# Revit family: xJWELED 40M Exit Lighting Non-Hosted_R16
name_source: partatom
category: Lighting Fixtures
revit_build: Autodesk Revit 2016 (Build: 20151007_0715(x64)
units: mm (PartAtom-declared; Revit-internal decimal feet)

## family parameters
Always vertical = Yes
Cut with Voids When Loaded = No
Light Source = Yes
OmniClass Number = 23.80.70.00
OmniClass Title = Lighting
Part Type = Normal
Room Calculation Point = No
Round Connector Dimension = Use Diameter
Shared = No
Work Plane-Based = No

## types (14) — shared parameters
AS2293 Classification = C0=E1.6 C90=E1.25
Base Material Construction = Polycarbonate
Color Filter = 16777215
Cover Material Construction = Clear Polycarbonate
Diffuser = Opal panel
Dimensions (L x W x H) = 560mm x 130mm x 280mm
Dimming Lamp Color Temperature Shift = <None>
Emit Shape Visible in Rendering = No
IK Rating = IK08 (side surface) IK09 (front surface)
IP Rating = IP66/67
Lamp = 4 x 5 high intensity, low energy LED, surface mounted onto a replaceable lamp bar - 100,000hr
Manufacturer = Clevertronics
Mounting = Wall mount
Operating Temperature = 0°C to 40°C
Operating Voltage = 240V AC; 50Hz
Photometric Web File = ll18428a - LJWELED-40-WM-RR.IES
Replacement Emergency Lamp = 8002122 PCA:Duris E5 LED Strip 5LED ,CT10152-D4
Tilt Angle = 0.00°
Total Lumen Output = 74.1
Viewing Distance = 40m
Weight = 5.5Kg

## per-type parameters (varying)
| type | Battery | Battery Type | Charging Method | Description | MIC Number | Operating Mode | Pictogram | Power Consumption | Power Consumption (Standby) | Product Description | Replacement Battery | Replacement Emergency Driver | Testing Node | Testing System |
| LJWELED-40-DALI-WM-E | Lithium Nanophosphate | 3.3V 2500mAh | Intelligent current limited constant voltage | WP LED Exit, WM, MNT,Exit,Dali Reg,L10,40mtr | AUA01220030102 | Maintained | EXIT wording (must specify user combination) | 5.3W | 2.8W | L10 Lithium Nanophosphate wall mount IP66/67 Jumbo weatherproof Exit | 1530010  BATTERY:L10 3.3V 2.5AH 200mm lead, Brkt | LJWELED-40-CKIT  WP LED Exit, Control Kit, L10, OWC | 8003060  PCA: New DALI #CT10629-Ax | DALI registered |
| LJWELED-40-DALI-WM-R | Lithium Nanophosphate | 3.3V 2500mAh | Intelligent current limited constant voltage | WP LED Exit, WM, MNT,RM, Dali Reg,L10, 40mtr | AUA01220040102 | Maintained | Running man (must specify user combination) | 5.3W | 2.8W | L10 Lithium Nanophosphate wall mount IP66/67 Jumbo weatherproof Exit | 1530010  BATTERY:L10 3.3V 2.5AH 200mm lead, Brkt | LJWELED-40-CKIT  WP LED Exit, Control Kit, L10, OWC | 8003060  PCA: New DALI #CT10629-Ax | DALI registered |
| LJWELED-40-DALI-WM-RR-UPS |  |  |  | WP LED Exit, WM, MNT, Dali Reg,RM>,UPS,40mtr | AUA01220080102 | Maintained with no integral battery backup (UPS) | Running man, Right arrow (must specify diffuser combination) | 2.8W |  | Wall mount IP66/67 Jumbo weatherproof Exit. Supplied from a UPS (240VAC) or 
220/240VAC/DC changeover supply (NOTE: change over facilities are required external to the luminaire supplied by others) |  | LJWELED-40-CKIT-DALI-UPS  WP LED Exit, Control Kit, Dali Reg, UPS | 8003060  PCA: New DALI #CT10629-Ax | DALI registered |
| LJWELED-40-DALI-WM-R-UPS |  |  |  | WP LED Exit, WM, MNT, Dali Reg,RM,UPS, 40mtr | AUA01220090102 | Maintained with no integral battery backup (UPS) | Running man | 2.8W |  | Wall Mount IP66/67 Jumbo Weatherproof Exit 
Supplied from a UPS (240VAC) or 220/240VAC changeover supply (NOTE: change over facilities are required external to the luminaire supplied by others) |  | AUM01270090102 LJWELED-40-CKIT-DALI-UPS   WP LED Exit, Control Kit, Dali Reg, UPS | 8003060  PCA: New DALI #CT10629-Ax | DALI registered |
| LJWELED-40-DALI-WM-TP-R | 3.3V 2500mAh | Lithium Nanophosphate | Intelligent current limited constant voltage | WP LED Exit, WM, MNT, Dali Reg, RM, 40mtr | AUA01240010102 | Maintained | Running man (Must specify diffuser combination) | 5.3W | 2.8W | L10 Lithium Nanophosphate wall mount IP66/67 Jumbo weatherproof Exit with tamperproof screws | 1530010 BATTERY:L10 3.3V 2.5AH 200mm lead, BRKT. | LJWELED-40-CKIT WP LED Exit, Control Kit, L10 | 8003060  PCA: New DALI #CT10629-Ax | DALI registered |
| LJWELED-40-DALI-WM-TP-RL | 3.3V 2500mAh | Lithium Nanophosphate | Intelligent current limited constant voltage | WP LED Exit, WM, MNT, Dali Reg, <RM, 40mtr | AUA01240020102 | Maintained | Running man, Left arrow (Must specify diffuser combination) | 5.3W | 2.8W | L10 Lithium Nanophosphate wall mount IP66/67 Jumbo weatherproof Exit with tamperproof screws | 1530010 BATTERY:L10 3.3V 2.5AH 200mm lead, BRKT. | LJWELED-40-CKIT WP LED Exit, Control Kit, L10 | 8003060  PCA: New DALI #CT10629-Ax | DALI registered |
| LJWELED-40-DALI-WM-TP-RR | 3.3V 2500mAh | Lithium Nanophosphate | Intelligent current limited constant voltage | WP LED Exit, WM, MNT, Dali Reg, RM>, 40mtr | AUA01240030102 | Maintained | Running man, Right arrow (Must specify diffuser combination) | 5.3W | 2.8W | L10 Lithium Nanophosphate wall mount IP66/67 Jumbo weatherproof Exit with tamperproof screws | 1530010 BATTERY:L10 3.3V 2.5AH 200mm lead, BRKT. | LJWELED-40-CKIT WP LED Exit, Control Kit, L10 | 8003060  PCA: New DALI #CT10629-Ax | DALI registered |
| LJWELED-40-HV-WM-R | 3.3V 2500mAh | Lithium Nanophosphate | Intelligent current limited constant voltage | WP LED Exit, WM, MNT, Dali Reg, RM>, 40mtr | AUA01820020001 | Maintained | Running man, (Must specify diffuser combination) | 5.3W | 2.8W | L10 Optimum Wall Mount IP66/67 Jumbo Weatherproof Exit | 1530010 BATTERY:L10 3.3V 2.5AH 200mm lead, BRKT. | AUM01870050001  LJWELED-40-CKIT-HV  WP LED Exit, Control Kit, L10, HV (incl. Hive node) | 8003191 PCA: RF Node CT10678-A12 Int Antenna LLPro | Zoneworks XT HIVE (RF) |
| LJWELED-40-HV-WM-RL | 3.3V 2500mAh | Lithium Nanophosphate | Intelligent current limited constant voltage | WP LED Exit, WM, MNT, <RM, L10, HV, 40mtr | AUA01820040001 | Maintained | Running man, Left arrow (Must specify diffuser combination) | 5.3W | 2.8W | L10 Optimum Wall Mount IP66/67 Jumbo Weatherproof Exit | 1530010 BATTERY:L10 3.3V 2.5AH 200mm lead, BRKT. | AUM01870050001  LJWELED-40-CKIT-HV  WP LED Exit, Control Kit, L10, HV (incl. Hive node) | 8003191 PCA: RF Node CT10678-A12 Int Antenna LLPro | Zoneworks XT HIVE (RF) |
| LJWELED-40-HV-WM-RR | 3.3V 2500mAh | Lithium Nanophosphate | Intelligent current limited constant voltage | WP LED Exit, WM, MNT, RM>, L10, HV, 40mtr | AUA01820030001 | Maintained | Running man, Right arrow (Must specify diffuser combination) | 5.3W | 2.8W | L10 Optimum Wall Mount IP66/67 Jumbo Weatherproof Exit | 1530010 BATTERY:L10 3.3V 2.5AH 200mm lead, BRKT. | AUM01870050001  LJWELED-40-CKIT-HV  WP LED Exit, Control Kit, L10, HV (incl. Hive node) | 8003191 PCA: RF Node CT10678-A12 Int Antenna LLPro | Zoneworks XT HIVE (RF) |
| LJWELED-40-WM-R | 3.3V 2500mAh | Lithium Nanophosphate | Intelligent current limited constant voltage | WP LED Exit, WM, MNT, RM, L10, 40mtr, CTP, OWC | AUA01320030001 | Maintained | Running man (Must specify diffuser combination) | 5.3W | 2.8W | L10 Optimum Wall Mount IP66/67 Jumbo Weatherproof Exit, Enabled with Clevertest Plus | 1530010 BATTERY:L10 3.3V 2.5AH 200mm lead, BRKT. | AUM01370060001 LJWELED-40-CKIT WP LED Exit, Control Kit, L10, OWC |  | Clevertest Plus Enabled (Not activated by default) |
| LJWELED-40-WM-RL | 3.3V 2500mAh | Lithium Nanophosphate | Intelligent current limited constant voltage | WP LED Exit, WM, MNT, <RM, L10, 40mtr, CTP, OWC | AUA01320050001 | Maintained | Running man, Left arrow (Must specify diffuser combination) | 5.3W | 2.8W | L10 Optimum Wall Mount IP66/67 Jumbo Weatherproof Exit, Enabled with Clevertest Plus | 1530010 BATTERY:L10 3.3V 2.5AH 200mm lead, BRKT. | AUM01370060001 LJWELED-40-CKIT WP LED Exit, Control Kit, L10, OWC |  | Clevertest Plus Enabled (Not activated by default) |
| LJWELED-40-WM-RR | 3.3V 2500mAh | Lithium Nanophosphate | Intelligent current limited constant voltage | WP LED Exit, WM, MNT, RM>, L10, 40mtr, CTP, OWC | AUA01320040001 | Maintained | Running man, Right arrow (Must specify diffuser combination) | 5.3W | 2.8W | L10 Optimum Wall Mount IP66/67 Jumbo Weatherproof Exit, Enabled with Clevertest Plus | 1530010 BATTERY:L10 3.3V 2.5AH 200mm lead, BRKT. | AUM01370060001 LJWELED-40-CKIT WP LED Exit, Control Kit, L10, OWC |  | Clevertest Plus Enabled (Not activated by default) |
| LJWELED-40-WM-SP-UPS | 3.3V 2500mAh | Lithium Nanophosphate | Intelligent current limited constant voltage | WP LED Exit, WM, MNT, SP, UPS, 40mtr | AUA01520010001 | If a 240V AC supply is applied to the luminaire the LED lamp will illuminate. To operate the fitting in Non-Maintained mode an external sensing relay (supplied by others) will be required to sense the loss of supply to the local lighting circuit and facilitate the changeover to the 240V AC backup/UPS supply | Customised diffuser, needs to be specified on order | 5.3W |  | Wall Mount IP66/67 Jumbo LED Weatherproof Custom Sign. Supplied from a UPS 
(240VAC) or 220/240VAC changeover supply (NOTE: change over facilities are required external to the luminaire supplied by others). |  | LJWELED-40-CKIT-UPS WP LED Exit, Control Kit, UPS |  |  |

note: column(s) folded — value = type name in every type: Model

## geometry (parser evidence)
native form markers: Sweep x2
no freeform markers — native parametric forms only
